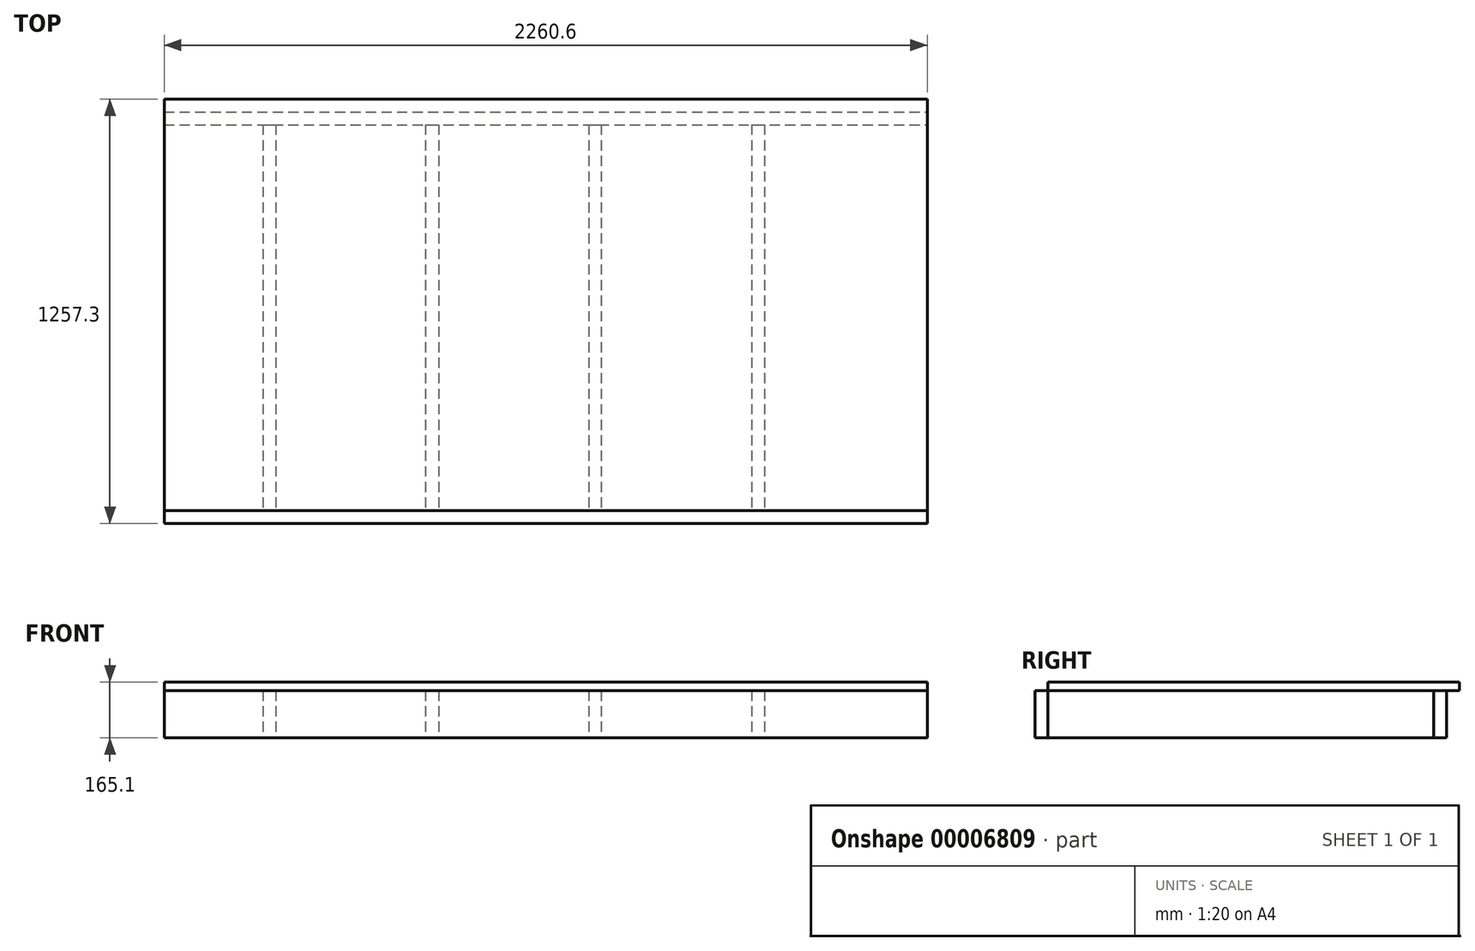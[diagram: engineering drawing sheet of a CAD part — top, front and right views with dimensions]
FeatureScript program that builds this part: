
annotation { "Feature Type Name" : "Feature", "Feature Type Description" : "" }
export const myFeature = defineFeature(function(context is Context, id is Id, definition is map)
    precondition{}
    {
        {
            var Q0;
            Q0=qCreatedBy(makeId("Top.planeOp"),FACE);
            var sketch = newSketch(context, id + "F0", { "sketchPlane" : qUnion([Q0])});
            skLineSegment(sketch, "E0.rect.bottom", {"start": v(1130.3, 609.6) * mm, "end": v(-1130.3, 609.6) * mm, "construction": true});
            skLineSegment(sketch, "E0.rect.top", {"start": v(1130.3, -609.6) * mm, "end": v(-1130.3, -609.6) * mm, "construction": true});
            skLineSegment(sketch, "E0.rect.left", {"start": v(1130.3, 609.6) * mm, "end": v(1130.3, -609.6) * mm, "construction": true});
            skLineSegment(sketch, "E0.rect.right", {"start": v(-1130.3, 609.6) * mm, "end": v(-1130.3, -609.6) * mm, "construction": true});
            skPoint(sketch, "E0.rect.middle", {"position": v(0, 0) * mm});
            skLineSegment(sketch, "E1.bottom", {"start": v(-1130.3, -609.6) * mm, "end": v(1130.3, -609.6) * mm});
            skLineSegment(sketch, "E1.top", {"start": v(-1130.3, -571.5) * mm, "end": v(1130.3, -571.5) * mm});
            skLineSegment(sketch, "E1.left", {"start": v(-1130.3, -609.6) * mm, "end": v(-1130.3, -571.5) * mm});
            skLineSegment(sketch, "E1.right", {"start": v(1130.3, -609.6) * mm, "end": v(1130.3, -571.5) * mm});
            skLineSegment(sketch, "E2.bottom", {"start": v(-1130.3, 609.6) * mm, "end": v(1130.3, 609.6) * mm});
            skLineSegment(sketch, "E2.top", {"start": v(-1130.3, 571.5) * mm, "end": v(1130.3, 571.5) * mm});
            skLineSegment(sketch, "E2.left", {"start": v(-1130.3, 609.6) * mm, "end": v(-1130.3, 571.5) * mm});
            skLineSegment(sketch, "E2.right", {"start": v(1130.3, 609.6) * mm, "end": v(1130.3, 571.5) * mm});
            skLineSegment(sketch, "E3.bottom", {"start": v(-1130.3, 571.5) * mm, "end": v(-1092.2, 571.5) * mm});
            skLineSegment(sketch, "E3.top", {"start": v(-1130.3, -571.5) * mm, "end": v(-1092.2, -571.5) * mm});
            skLineSegment(sketch, "E3.left", {"start": v(-1130.3, 571.5) * mm, "end": v(-1130.3, -571.5) * mm});
            skLineSegment(sketch, "E3.right", {"start": v(-1092.2, 571.5) * mm, "end": v(-1092.2, -571.5) * mm});
            skLineSegment(sketch, "E4.bottom", {"start": v(1130.3, 571.5) * mm, "end": v(1092.2, 571.5) * mm});
            skLineSegment(sketch, "E4.top", {"start": v(1130.3, -571.5) * mm, "end": v(1092.2, -571.5) * mm});
            skLineSegment(sketch, "E4.left", {"start": v(1130.3, 571.5) * mm, "end": v(1130.3, -571.5) * mm});
            skLineSegment(sketch, "E4.right", {"start": v(1092.2, 571.5) * mm, "end": v(1092.2, -571.5) * mm});
            skLineSegment(sketch, "E5.1.0.0", {"start": v(647.7, 571.5) * mm, "end": v(647.7, -571.5) * mm});
            skLineSegment(sketch, "E5.1.0.1", {"start": v(609.6, 571.5) * mm, "end": v(609.6, -571.5) * mm});
            skLineSegment(sketch, "E5.2.0.0", {"start": v(165.1, 571.5) * mm, "end": v(165.1, -571.5) * mm});
            skLineSegment(sketch, "E5.2.0.1", {"start": v(127, 571.5) * mm, "end": v(127, -571.5) * mm});
            skLineSegment(sketch, "E5.3.0.0", {"start": v(-317.5, 571.5) * mm, "end": v(-317.5, -571.5) * mm});
            skLineSegment(sketch, "E5.3.0.1", {"start": v(-355.6, 571.5) * mm, "end": v(-355.6, -571.5) * mm});
            skLineSegment(sketch, "E5.4.0.0", {"start": v(-800.1, 571.5) * mm, "end": v(-800.1, -571.5) * mm});
            skLineSegment(sketch, "E5.4.0.1", {"start": v(-838.2, 571.5) * mm, "end": v(-838.2, -571.5) * mm});
            skLineSegment(sketch, "E5.direction1", {"start": v(1130.3, -571.5) * mm, "end": v(647.7, -571.5) * mm, "construction": true});
            skSolve(sketch);
        }
        {
            var Q0;
            Q0=makeQuery(id+"F0.imprint","IMPRINT",FACE,{"disambiguationData":[TD([[makeQuery(id+"F0.imprint","IMPRINT",EDGE,{"derivedFrom":sQuery(id+"F0.wireOp",EDGE,"E2.bottom")}),-1.0]])]});
            var Q1;
            Q1=makeQuery(id+"F0.imprint","IMPRINT",FACE,{"disambiguationData":[TD([[makeQuery(id+"F0.imprint","IMPRINT",EDGE,{"derivedFrom":sQuery(id+"F0.wireOp",EDGE,"E1.bottom")}),1.0]])]});
            extrude(context, id + "F1", {"entities" : qUnion([Q0, Q1]), "depth" : 139.7 * mm});
        }
        {
            var Q0;
            Q0=makeQuery(id+"F0.imprint","IMPRINT",FACE,{"disambiguationData":[TD([[makeQuery(id+"F0.imprint","IMPRINT",EDGE,{"derivedFrom":sQuery(id+"F0.wireOp",EDGE,"E3.bottom")}),-1.0]])]});
            var Q1;
            {var subQ1=sQuery(id+"F0.wireOp",EDGE,"E5.4.0.0");Q1=makeQuery(id+"F0.imprint","IMPRINT",FACE,{"disambiguationData":[TD([[makeQuery(id+"F0.imprint","IMPRINT",EDGE,{"derivedFrom":subQ1}),-1.0]])]});}
            var Q2;
            {var subQ1=sQuery(id+"F0.wireOp",EDGE,"E5.3.0.0");Q2=makeQuery(id+"F0.imprint","IMPRINT",FACE,{"disambiguationData":[TD([[makeQuery(id+"F0.imprint","IMPRINT",EDGE,{"derivedFrom":subQ1}),-1.0]])]});}
            var Q3;
            {var subQ1=sQuery(id+"F0.wireOp",EDGE,"E5.2.0.0");Q3=makeQuery(id+"F0.imprint","IMPRINT",FACE,{"disambiguationData":[TD([[makeQuery(id+"F0.imprint","IMPRINT",EDGE,{"derivedFrom":subQ1}),-1.0]])]});}
            var Q4;
            {var subQ1=sQuery(id+"F0.wireOp",EDGE,"E5.1.0.0");Q4=makeQuery(id+"F0.imprint","IMPRINT",FACE,{"disambiguationData":[TD([[makeQuery(id+"F0.imprint","IMPRINT",EDGE,{"derivedFrom":subQ1}),-1.0]])]});}
            var Q5;
            Q5=makeQuery(id+"F0.imprint","IMPRINT",FACE,{"disambiguationData":[TD([[makeQuery(id+"F0.imprint","IMPRINT",EDGE,{"derivedFrom":sQuery(id+"F0.wireOp",EDGE,"E4.bottom")}),1.0]])]});
            extrude(context, id + "F2", {"entities" : qUnion([Q0, Q1, Q2, Q3, Q4, Q5]), "depth" : 139.7 * mm});
        }
        {
            var Q0;
            Q0=makeQuery(id+"F1.opExtrude","CAP_FACE",FACE,{"disambiguationData":[OSD([sQuery(id+"F0.wireOp",EDGE,"E2.bottom"),sQuery(id+"F0.wireOp",EDGE,"E2.top"),sQuery(id+"F0.wireOp",EDGE,"E2.left"),sQuery(id+"F0.wireOp",EDGE,"E2.right"),sQuery(id+"F0.wireOp",EDGE,"E3.bottom"),sQuery(id+"F0.wireOp",EDGE,"E4.bottom")])],"isStart":false});
            var sketch = newSketch(context, id + "F3", { "sketchPlane" : qUnion([Q0])});
            skLineSegment(sketch, "E6.bottom", {"start": v(-1130.3, 647.7) * mm, "end": v(1130.3, 647.7) * mm});
            skLineSegment(sketch, "E6.top", {"start": v(-1130.3, -571.5) * mm, "end": v(1130.3, -571.5) * mm});
            skLineSegment(sketch, "E6.left", {"start": v(-1130.3, 647.7) * mm, "end": v(-1130.3, -571.5) * mm});
            skLineSegment(sketch, "E6.right", {"start": v(1130.3, 647.7) * mm, "end": v(1130.3, -571.5) * mm});
            skLineSegment(sketch, "E7.bottom", {"start": v(-1130.3, -571.5) * mm, "end": v(-1003.3, -571.5) * mm});
            skLineSegment(sketch, "E7.top", {"start": v(-1130.3, -482.6) * mm, "end": v(-1003.3, -482.6) * mm});
            skLineSegment(sketch, "E7.left", {"start": v(-1130.3, -571.5) * mm, "end": v(-1130.3, -482.6) * mm});
            skLineSegment(sketch, "E7.right", {"start": v(-1003.3, -571.5) * mm, "end": v(-1003.3, -482.6) * mm});
            skLineSegment(sketch, "E8", {"start": v(0, 647.7) * mm, "end": v(0, -461.56) * mm, "construction": true});
            skLineSegment(sketch, "E9.0.MirrorCS", {"start": v(1003.3, -571.5) * mm, "end": v(1003.3, -482.6) * mm});
            skLineSegment(sketch, "E9.1.MirrorCS", {"start": v(1130.3, -571.5) * mm, "end": v(1130.3, -482.6) * mm});
            skLineSegment(sketch, "E9.2.MirrorCS", {"start": v(1130.3, -482.6) * mm, "end": v(1003.3, -482.6) * mm});
            skLineSegment(sketch, "E9.3.MirrorCS", {"start": v(1130.3, -571.5) * mm, "end": v(1003.3, -571.5) * mm});
            skLineSegment(sketch, "E9.5.MirrorCS", {"start": v(1130.3, -571.5) * mm, "end": v(-1130.3, -571.5) * mm});
            skSolve(sketch);
        }
        {
            var Q0;
            {var subQ6=sQuery(id+"F3.wireOp",EDGE,"E6.top");Q0=makeQuery(id+"F3.imprint","IMPRINT",FACE,{"disambiguationData":[TD([[makeQuery(id+"F3.imprint","IMPRINT",EDGE,{"derivedFrom":subQ6}),1.0]])]});}
            var Q1;
            {var subQ5=sQuery(id+"F3.wireOp",EDGE,"E6.bottom");Q1=makeQuery(id+"F3.imprint","IMPRINT",FACE,{"disambiguationData":[TD([[makeQuery(id+"F3.imprint","IMPRINT",EDGE,{"derivedFrom":subQ5}),-1.0]])]});}
            var Q2;
            {var subQ3=sQuery(id+"F3.wireOp",EDGE,"E6.left");var subQ5=makeQuery(id+"F1.opExtrude","CAP_EDGE",EDGE,{"disambiguationData":[OSD([sQuery(id+"F0.wireOp",EDGE,"E2.bottom")])],"isStart":false});var subQ7=makeQuery(id+"F3.imprint","INTERSECT",VERTEX,{"derivedFrom":[subQ5,subQ3]});Q2=makeQuery(id+"F3.imprint","IMPRINT",FACE,{"disambiguationData":[TD([[makeQuery(id+"F3.imprint","IMPRINT",EDGE,{"disambiguationData":[TD([[subQ7,-1.0]])],"derivedFrom":subQ5}),-1.0]])]});}
            var Q3;
            {var subQ6=sQuery(id+"F3.wireOp",EDGE,"E7.top");Q3=makeQuery(id+"F3.imprint","IMPRINT",FACE,{"disambiguationData":[TD([[makeQuery(id+"F3.imprint","IMPRINT",EDGE,{"derivedFrom":subQ6}),1.0]])]});}
            extrude(context, id + "F4", {"entities" : qUnion([Q0, Q1, Q2, Q3]), "depth" : 25.4 * mm});
        }
    });
